# Revit family: Bticino_Lighting_Management_Standalone_Motion_Sensor_Ceiling
name_source: partatom
category: Dispositifs d'éclairage
units: mm (PartAtom-declared; Revit-internal decimal feet)

## family parameters
Conserver l'orientation des annotations = Non
Cote de connecteur circulaire = Utiliser le diamètre
Couper avec des vides une fois chargée = Non
Hôte = Face
Partagée = Non
Point de calcul de pièce = Non
Type d'élément = Normal

## types (2) — shared parameters
Alarm function = Non
Collecteur de terre = Non
Colour = White
Constant light control = Oui
Cosses d'artère secondaire = Non
Detection angle horizontal (MAX) (°) = 360
Detection angle horizontal (MIN) (°) = 360
Diameter detection range on floor (m) = 8
Elévation par défaut = 1219 mm
Fabricant = Bticino
Fonction variateur intégré = Non
Forced switch off = Non
Frequency (MAX) (Hz) = 60
Frequency (MIN) (Hz) = 50
General Conditions of Use = https://export.legrand.com
HVAC-control = Non
Liaison neutre = Non
Max. duty cycle (mn) = 10
Maximum mounting height (m) = 2.5
Nominal voltage (V) = 240
RAL-number (akin) = 9006
Remote operation = Non
Response value luminosity (MAX) (lx) = 1275
Response value luminosity (MIN) (lx) = 10
Response value luminosity adjustable = Oui
Response value sensitivity adjustable = Oui
Substation input = Non
Suitable for wireless transmission = Non
Temperature (MAX) (°C) = 35
Temperature (MIN) (°C) = -5
URL = http://www.legrandoc.com
Voltage type = AC
zero-valued in all types: Max. starting current (A), Max. switching power (W)

## per-type parameters (varying)
| type | Degree of protection (IP) | Description | Max. transmission range frontally (m) | Max. transmission range sideways (m) | Min. switch-on time (s) | Model | Modèle | Mounting method |
| PIR - Surface - 360° - 45m² | IP20 | PIR 360° SENSOR CEILING SURFACE MOUNTED | 8 | 8 | 10 | Presence detector | BMSA1205 | Surface mounted (plaster) |
| PIR-Ceiling-360° | IP41 | 360° motion sensor - IP 41 - 8 m - ceiling-mounting - PIR technology - blister | 4 | 4 | 5 | Movement sensor | BMSA1204 | Flush mounted (plaster) |

## geometry (parser evidence)
native form markers: Blend x10
no freeform markers — native parametric forms only
